# Revit family: Metal_See_Through_Lockers-Salsbury_Industries-S_63000_Series-3_Wide_Units
name_source: partatom
category: Specialty Equipment
units: mm (PartAtom-declared; Revit-internal decimal feet)

## family parameters
Always vertical = Yes
Classification Number = 23.40.00.00
Cut with Voids When Loaded = No
Enable Cutting in Views = No
Maintain Annotation Orientation = No
Part Type = Normal
Room Calculation Point = No
Round Connector Dimension = Use Diameter
Shared = No
Work Plane-Based = No

## types (18) — shared parameters
Assembly Code = C1030310
Building Codes = https://www.lockers.com
Construction Details = https://www.lockers.com
Door Window Width = 6.5 "
Green Building-LEED = https://www.arcat.com
Hasp Handle Material = Plastic - Salsbury Finish - Black
Hasp Plate Rivet Material = Steel -Salsbury Finish - Polished Steel
Installation-Fabrication = https://www.lockers.com
Keynote = 10 51 00
Manufacturer = Salsbury Industries
Manufacturer Fax = 1-800-562-5399
Manufacturer Website = https://www.lockers.com
MasterFormat Number = 10 51 13
MasterFormat Title = Lockers
OmniClass 23 Number = 23.40.00.00
Product Data = https://www.lockers.com
Revision = R1_2018-10
Sales Information = https://www.lockers.com
Specification = https://www.lockers.com
Test Data = https://www.lockers.com
Type Comments = See-Through Metal Lockers - Triple Tier
URL = www.lockers.com
Version = 3.0 (03/30/18)
Width = 36.04 "
Window Panel Material = Polycarbonate - Salsbury Finish - Clear
zero-valued in all types: Default Elevation

## per-type parameters (varying)
| type | Base Height | Compartment Divider Height | Depth | Description | Door Location D1 | Door Window Height | Door Window Offset | Individual Door Height | Model | OmniClass 23 Title | Sloping Hood Height | Standard Leg Base | Unit Height | Zee Base |
| S-63362 - with Standard 6" High Legs | 6 " | 22.814 " | 12.01 " | 3 Wide - 6 Feet High - 12 Inches Deep | See-Through Metal Locker Doors-12 inch with Hasps : Triple Tier Door - 6 foot | 5.25 " | 3.653 " | 23.189 " | S-63362 | Equipment and Furnishings | 6.625 " | Metal Locker Legs - 3 Wide : 6" High - 36" W x 12" D | 72 " | Metal Locker Zee Base - 3 Wide : None |
| S-63365 - with Standard 6" High Legs | 6 " | 22.814 " | 15.01 " | 3 Wide - 6 Feet High - 15 Inches Deep | See-Through Metal Locker Doors-12 inch with Hasps : Triple Tier Door - 6 foot | 5.25 " | 3.653 " | 23.189 " | S-63365 | Equipment and Furnishings | 8.682 " | Metal Locker Legs - 3 Wide : 6" High - 36" W x 15" D | 72 " | Metal Locker Zee Base - 3 Wide : None |
| S-63368 - with Standard 6" High Legs | 6 " | 22.814 " | 18.01 " | 3 Wide - 6 Feet High - 18 Inches Deep | See-Through Metal Locker Doors-12 inch with Hasps : Triple Tier Door - 6 foot | 5.25 " | 3.653 " | 23.189 " | S-63368 | Equipment and Furnishings | 10.739 " | Metal Locker Legs - 3 Wide : 6" High - 36"W x 18"D | 72 " | Metal Locker Zee Base - 3 Wide : None |
| S-63362 - with 77572 Zee Base and 77550 Lockers without Legs | 4 " | 22.814 " | 12.01 " | 3 Wide - 6 Feet High - 12 Inches Deep with Zee Base and Lockers without Legs | See-Through Metal Locker Doors-12 inch with Hasps : Triple Tier Door - 6 foot | 5.25 " | 3.653 " | 23.189 " | S-63362 with 77572 and 77550 | Equipment and Furnishings | 6.625 " | Metal Locker Legs - 3 Wide : No Legs | 72 " | Metal Locker Zee Base - 3 Wide : 77572- 36" W x 12" D |
| S-63365 - with 77575 Zee Base and 77550 Lockers without Legs | 4 " | 22.814 " | 15.01 " | 3 Wide - 6 Feet High - 15 Inches Deep with Zee Base and Lockers without Legs | See-Through Metal Locker Doors-12 inch with Hasps : Triple Tier Door - 6 foot | 5.25 " | 3.653 " | 23.189 " | S-63365 with 77575 and 77550 | Equipment and Furnishings | 8.682 " | Metal Locker Zee Base - 3 Wide : None | 72 " | Metal Locker Zee Base - 3 Wide : 77575 - 36" W x 15" D |
| S-63368 - with 77578 Zee Base and 77550 Lockers without Legs | 4 " | 22.814 " | 18.01 " | 3 Wide - 6 Feet High - 18 Inches Deep with Zee Base and Lockers without Legs | See-Through Metal Locker Doors-12 inch with Hasps : Triple Tier Door - 6 foot | 5.25 " | 3.653 " | 23.189 " | S-63368 with 77578 and 77550 | Equipment aqnd Furnishings | 10.739 " | Metal Locker Zee Base - 3 Wide : None | 72 " | Metal Locker Zee Base - 3 Wide : 77578 - 36"W x 18"D |
| S-63362 - with 77550 Lockers without Legs | 0 " | 22.814 " | 12.01 " | 3 Wide - 6 Feet High - 12 Inches Deep with Lockers without Legs | See-Through Metal Locker Doors-12 inch with Hasps : Triple Tier Door - 6 foot | 5.25 " | 3.653 " | 23.189 " | S-63362 with 77550 | Equipment and Furnishings | 6.625 " | Metal Locker Legs - 3 Wide : No Legs | 72 " | Metal Locker Zee Base - 3 Wide : None |
| S-63365 - with 77550 Lockers without Legs | 0 " | 22.814 " | 15.01 " | 3 Wide - 6 Feet High - 15 Inches Deep with Lockers without Legs | See-Through Metal Locker Doors-12 inch with Hasps : Triple Tier Door - 6 foot | 5.25 " | 3.653 " | 23.189 " | S-63365 with 77550 | Equipment and Furnishings | 8.682 " | Metal Locker Legs - 3 Wide : No Legs | 72 " | Metal Locker Zee Base - 3 Wide : None |
| S-63368 - with 77550 Lockers without Legs | 0 " | 22.814 " | 18.01 " | 3 Wide - 6 Feet High - 18 Inches Deep with Lockers without Legs | See-Through Metal Locker Doors-12 inch with Hasps : Triple Tier Door - 6 foot | 5.25 " | 3.653 " | 23.189 " | S-63368 with 77550 | Equipment and Furnishings | 10.739 " | Metal Locker Legs - 3 Wide : No Legs | 72 " | Metal Locker Zee Base - 3 Wide : None |
| S-63352 - with Standard 6" High Legs | 6 " | 18.814 " | 12.01 " | 3 Wide - 5 Feet High - 12 Inches Deep | See-Through Metal Locker Doors-12 inch with Hasps : Triple Tier Door - 5 foot | 3.5 " | 3.553 " | 19.189 " | S-63352 | Equipment and Furnishings | 6.625 " | Metal Locker Legs - 3 Wide : 6" High - 36" W x 12" D | 60 " | Metal Locker Zee Base - 3 Wide : None |
| S-63352 - with 77572 Zee Base and 77550 Lockers without Legs | 4 " | 18.814 " | 12.01 " | 3 Wide - 5 Feet High - 12 Inches Deep with Zee Base and Lockers without Legs | See-Through Metal Locker Doors-12 inch with Hasps : Triple Tier Door - 5 foot | 3.5 " | 3.553 " | 19.189 " | S-63352 with 77572 and 77550 | Equipment and Furnishings | 6.625 " | Metal Locker Legs - 3 Wide : No Legs | 60 " | Metal Locker Zee Base - 3 Wide : 77572- 36" W x 12" D |
| S-63352 - with 77550 Lockers without Legs | 0 " | 18.814 " | 12.01 " | 3 Wide - 5 Feet High - 12 Inches Deep with Lockers without Legs | See-Through Metal Locker Doors-12 inch with Hasps : Triple Tier Door - 5 foot | 3.5 " | 3.553 " | 19.189 " | S-63352 with 77550 | Equipment and Furnishings | 6.625 " | Metal Locker Legs - 3 Wide : No Legs | 60 " | Metal Locker Zee Base - 3 Wide : None |
| S-63355 - with Standard 6" High Legs | 6 " | 18.814 " | 15.01 " | 3 Wide - 5 Feet High - 15 Inches Deep | See-Through Metal Locker Doors-12 inch with Hasps : Triple Tier Door - 5 foot | 3.5 " | 3.553 " | 19.189 " | S-63355 | Equipment and Furnishings | 8.682 " | Metal Locker Legs - 3 Wide : 6" High - 36" W x 15" D | 60 " | Metal Locker Zee Base - 3 Wide : None |
| S-63355 - with 77575 Zee Base and 77550 Lockers without Legs | 4 " | 18.814 " | 15.01 " | 3 Wide - 5 Feet High - 15 Inches Deep with Zee Base and Lockers without Legs | See-Through Metal Locker Doors-12 inch with Hasps : Triple Tier Door - 5 foot | 3.5 " | 3.553 " | 19.189 " | S-63355 with 77575 and 77550 | Equipment and Furnishings | 8.682 " | Metal Locker Zee Base - 3 Wide : None | 60 " | Metal Locker Zee Base - 3 Wide : 77575 - 36" W x 15" D |
| S-63355 - with 77550 Lockers without Legs | 0 " | 18.814 " | 15.01 " | 3 Wide - 5 Feet High - 15 Inches Deep with Lockers without Legs | See-Through Metal Locker Doors-12 inch with Hasps : Triple Tier Door - 5 foot | 3.5 " | 3.553 " | 19.189 " | S-63355 with 77550 | Equipment and Furnishings | 8.682 " | Metal Locker Legs - 3 Wide : No Legs | 60 " | Metal Locker Zee Base - 3 Wide : None |
| S-63358 - with Standard 6" High Legs | 6 " | 18.814 " | 18.01 " | 3 Wide - 5 Feet High - 18 Inches Deep | See-Through Metal Locker Doors-12 inch with Hasps : Triple Tier Door - 5 foot | 3.5 " | 3.553 " | 19.189 " | S-63358 | Equipment and Furnishings | 10.739 " | Metal Locker Legs - 3 Wide : 6" High - 36"W x 18"D | 60 " | Metal Locker Zee Base - 3 Wide : None |
| S-63358 - with 77578 Zee Base and 77550 Lockers without Legs | 4 " | 18.814 " | 18.01 " | 3 Wide - 5 Feet High - 18 Inches Deep with Zee Base and Lockers without Legs | See-Through Metal Locker Doors-12 inch with Hasps : Triple Tier Door - 5 foot | 3.5 " | 3.553 " | 19.189 " | S-63358 with 77578 and 77550 | Equipment and Furnishings | 10.739 " | Metal Locker Zee Base - 3 Wide : None | 60 " | Metal Locker Zee Base - 3 Wide : 77578 - 36"W x 18"D |
| S-63358 - with 77550 Lockers without Legs | 0 " | 18.814 " | 18.01 " | 3 Wide - 5 Feet High - 18 Inches Deep with Lockers without Legs | See-Through Metal Locker Doors-12 inch with Hasps : Triple Tier Door - 5 foot | 3.5 " | 3.553 " | 19.189 " | S-63358 with 77550 | Equipment and Furnishings | 10.739 " | Metal Locker Legs - 3 Wide : No Legs | 60 " | Metal Locker Zee Base - 3 Wide : None |

## geometry (parser evidence)
native form markers: Sweep x38
no freeform markers — native parametric forms only
